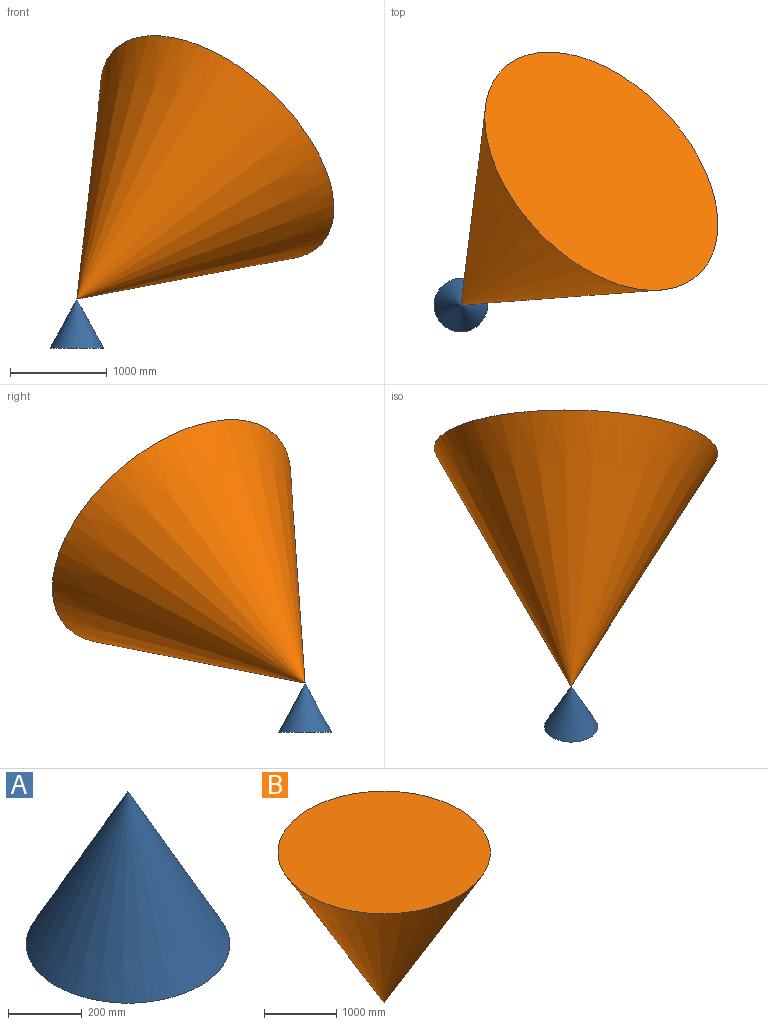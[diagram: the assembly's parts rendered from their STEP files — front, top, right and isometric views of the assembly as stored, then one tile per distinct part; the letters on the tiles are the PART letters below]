
ASSEMBLY  parts=2 mates=1
PART A: 2 faces, bbox 552.1x552.1x508 mm
  f0: cone r=276.07mm half-angle=28.5deg, axis (0,0,-1), area 501444.7mm2, adj f1
  f1: plane 552.14x552.14mm, normal (0,0,-1), area 239435.1mm2, adj f0
PART B: 2 faces, bbox 2932.9x2932.9x2540 mm
  f0: cone r=1466.47mm half-angle=30deg, axis (0,0,1), area 13512199.4mm2, adj f1
  f1: plane 2932.94x2932.94mm, normal (0,0,1), area 6756099.7mm2, adj f0
PLACE A t=(-320.02,12.47,1741.03)mm fixed
PLACE B rot(axis=(-0.7,0.71,-0.03),52deg) t=(1465.2,-2230.45,-2060.65)mm
MATE ball B.f0 <-> A.f0  axis (0.57,0.54,0.62) through (-320.02,12.47,1741.03)mm
